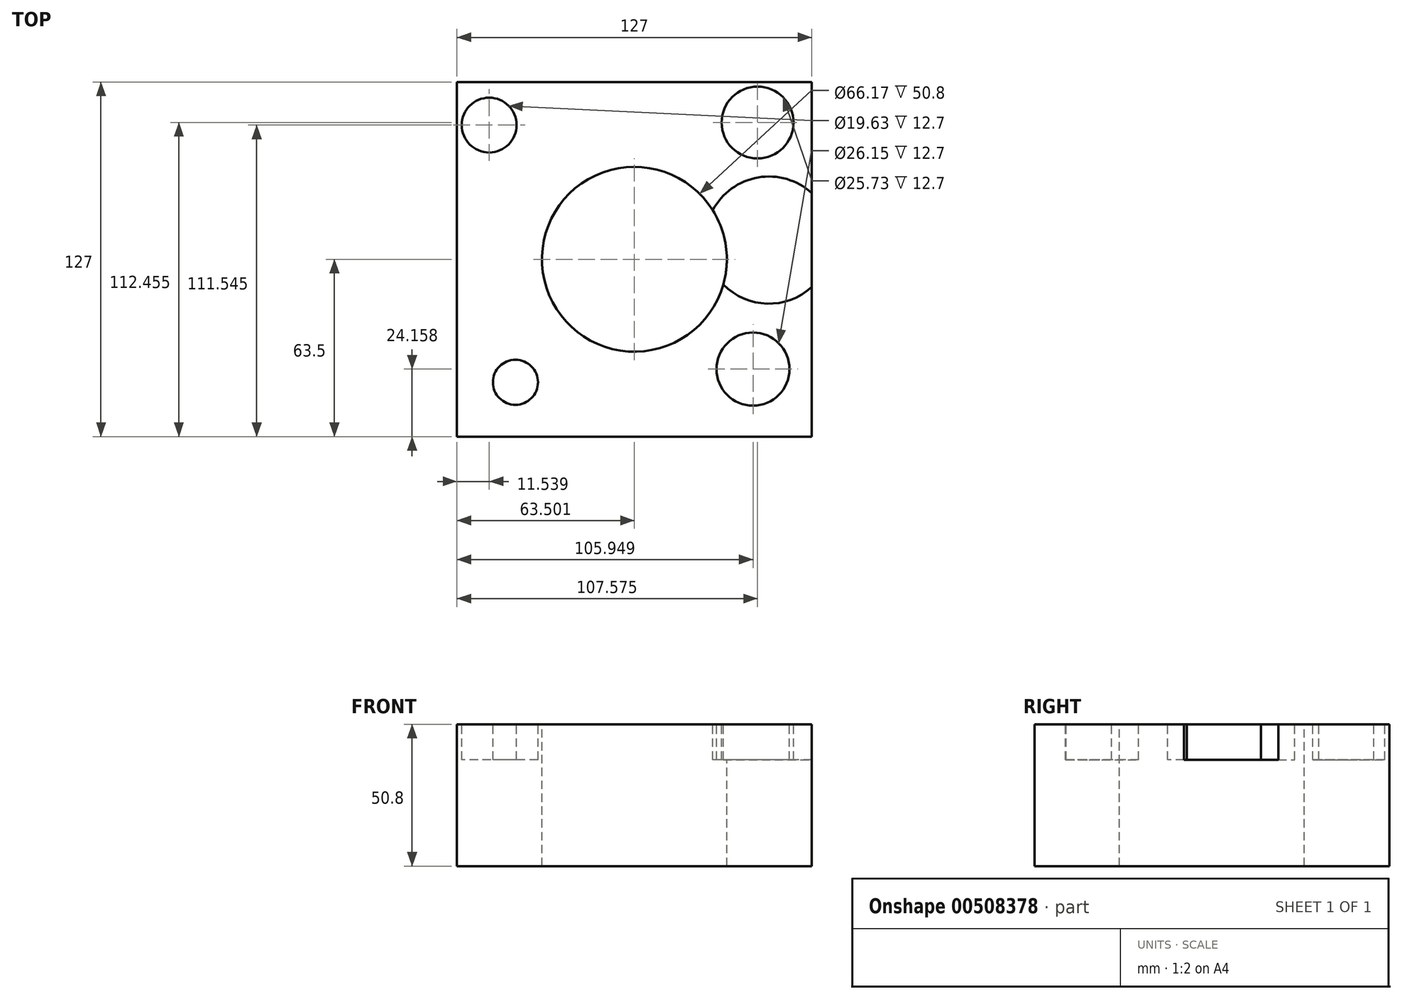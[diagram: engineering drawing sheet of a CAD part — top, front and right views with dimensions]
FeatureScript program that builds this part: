
annotation { "Feature Type Name" : "Feature", "Feature Type Description" : "" }
export const myFeature = defineFeature(function(context is Context, id is Id, definition is map)
    precondition{}
    {
        {
            var Q0;
            Q0=qCreatedBy(makeId("Top.planeOp"),FACE);
            var sketch = newSketch(context, id + "F0", { "sketchPlane" : qUnion([Q0])});
            skLineSegment(sketch, "E0.bottom", {"start": v(-62.56, -70.36) * mm, "end": v(64.44, -70.36) * mm});
            skLineSegment(sketch, "E0.top", {"start": v(-62.56, 56.64) * mm, "end": v(64.44, 56.64) * mm});
            skLineSegment(sketch, "E0.left", {"start": v(-62.56, -70.36) * mm, "end": v(-62.56, 56.64) * mm});
            skLineSegment(sketch, "E0.right", {"start": v(64.44, -70.36) * mm, "end": v(64.44, 56.64) * mm});
            skSolve(sketch);
        }
        {
            var Q0;
            Q0 = qSketchRegion(id + "F0", true);
            extrude(context, id + "F1", {"entities" : qUnion([Q0]), "depth" : 50.8 * mm});
        }
        {
            var Q0;
            Q0=makeQuery(id+"F1.opExtrude","CAP_FACE",FACE,{"disambiguationData":[OSD([sQuery(id+"F0.wireOp",EDGE,"E0.bottom"),sQuery(id+"F0.wireOp",EDGE,"E0.top"),sQuery(id+"F0.wireOp",EDGE,"E0.left"),sQuery(id+"F0.wireOp",EDGE,"E0.right")])],"isStart":false});
            var sketch = newSketch(context, id + "F2", { "sketchPlane" : qUnion([Q0])});
            skCircle(sketch, "E1", {"center": v(0.94, -6.86) * mm, "radius": 33.08 * mm});
            skPoint(sketch, "E1.centerSnap0", {"position": v(64.44, -6.86) * mm});
            skSolve(sketch);
        }
        {
            var Q0;
            Q0=makeQuery(id+"F2.imprint","IMPRINT",FACE,{"disambiguationData":[TD([[makeQuery(id+"F2.imprint","IMPRINT",EDGE,{"derivedFrom":sQuery(id+"F2.wireOp",EDGE,"E1")}),1.0]])]});
            extrude(context, id + "F3", {"entities" : qUnion([Q0]), "operationType" : NewBodyOperationType.REMOVE, "endBound" : BoundingType.THROUGH_ALL, "oppositeDirection" : true, "depth" : 25.4 * mm});
        }
        {
            var Q0;
            Q0=makeQuery(id+"F2.imprint","IMPRINT",FACE,{"disambiguationData":[TD([[makeQuery(id+"F2.imprint","IMPRINT",EDGE,{"derivedFrom":sQuery(id+"F2.wireOp",EDGE,"E1")}),-1.0]])]});
            var sketch = newSketch(context, id + "F4", { "sketchPlane" : qUnion([Q0])});
            skCircle(sketch, "E2", {"center": v(-51.02, 41.18) * mm, "radius": 9.81 * mm});
            skCircle(sketch, "E3", {"center": v(45.02, 42.1) * mm, "radius": 12.87 * mm});
            skCircle(sketch, "E4", {"center": v(-41.63, -50.91) * mm, "radius": 8.07 * mm});
            skCircle(sketch, "E5", {"center": v(43.39, -46.2) * mm, "radius": 13.07 * mm});
            skCircle(sketch, "E6", {"center": v(49.1, 0) * mm, "radius": 22.77 * mm});
            skSolve(sketch);
        }
        {
            var Q0;
            Q0 = qSketchRegion(id + "F4", true);
            extrude(context, id + "F5", {"entities" : qUnion([Q0]), "operationType" : NewBodyOperationType.REMOVE, "oppositeDirection" : true, "depth" : 12.7 * mm});
        }
    });
